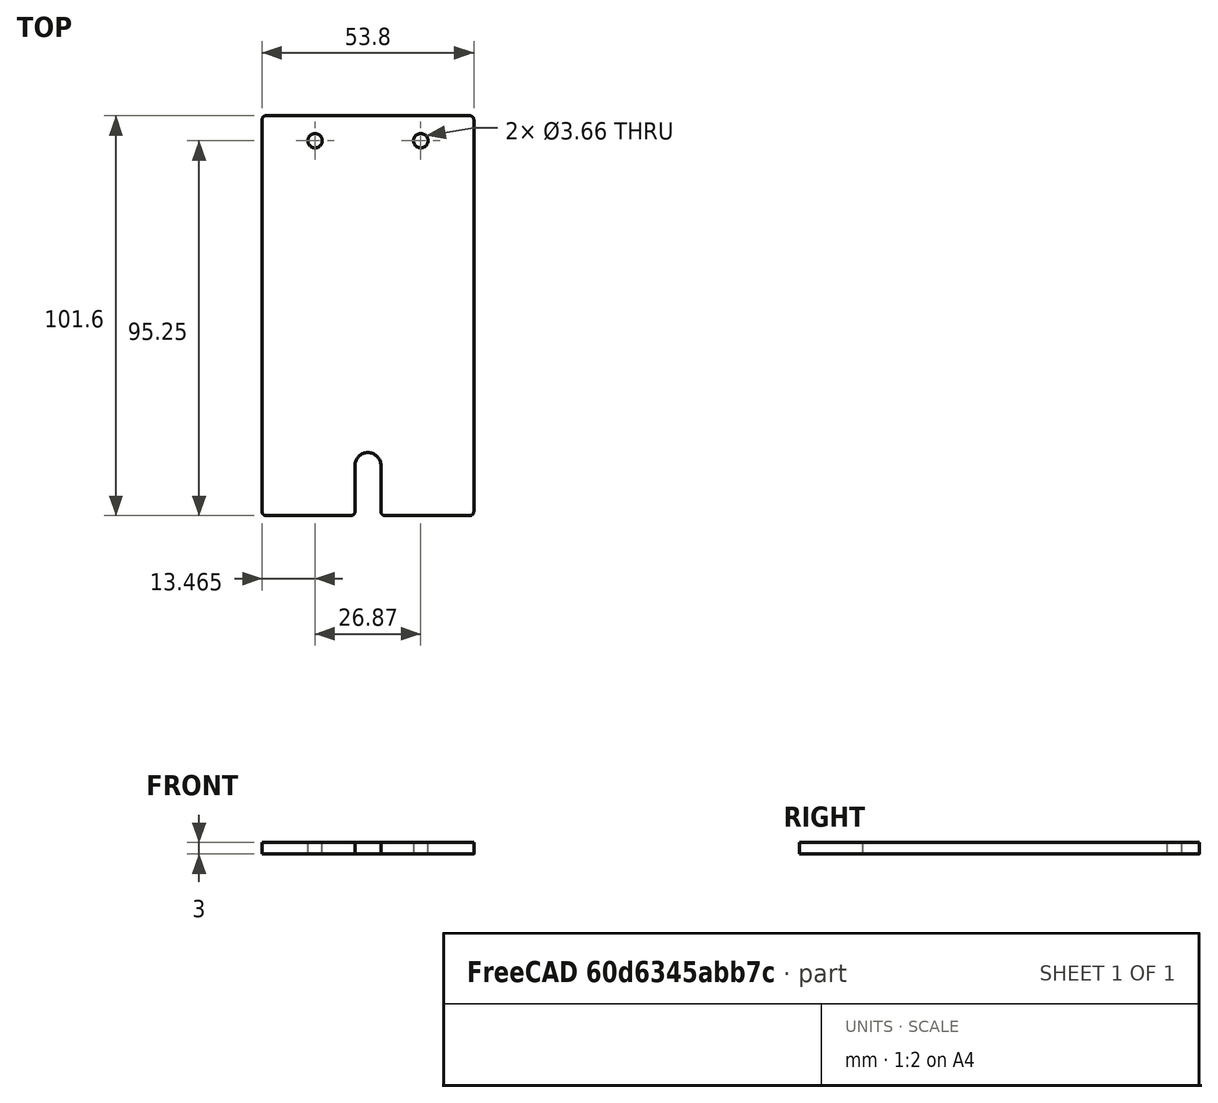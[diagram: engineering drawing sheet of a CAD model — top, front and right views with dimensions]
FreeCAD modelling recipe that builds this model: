
FCSTD DOCUMENT  (FreeCAD 0.21R33675 (Git))
Label: feeding_box_front
License: All rights reserved
LicenseURL: http://en.wikipedia.org/wiki/All_rights_reserved
objects: Sketcher::SketchObject×1, Spreadsheet::Sheet×1, PartDesign::Pad×1, PartDesign::Body×1
note: 4 computed .brp shape members not serialized (recipe doc carries the construction recipe); baked Part::Feature solids carry a one-line shape summary decoded from their .brp

FEATURE [Sketcher::SketchObject] Sketch
  FullyConstrained = true
  MapMode = 5
  Support = -> [XY_Plane]
  expr: Constraints[19] = Spreadsheet.FilletRadius
  expr: Constraints[21] = Spreadsheet.Height
  expr: Constraints[22] = Spreadsheet.Length
  expr: Constraints[26] = Spreadsheet.MountHoleDistanceFromBottom
  expr: Constraints[27] = Spreadsheet.MountHoleDiameter
  expr: Constraints[31] = Spreadsheet.BracketHoleFromSide
  expr: Constraints[32] = Spreadsheet.UpperBracketHoleFromTop
  expr: Constraints[41] = Spreadsheet.BracketHoleDiameter
  expr: Constraints[68] = Spreadsheet.BracketHoleFromSide
  expr: Constraints[72] = Spreadsheet.UpperBracketHoleFromTop
  expr: Constraints[74] = Spreadsheet.BracketHoleDiameter
  sketch-geometry (30):
    g0: ArcOfCircle CenterX=-25.9 CenterY=49.8 CenterZ=0 NormalX=0 NormalY=0 NormalZ=1 AngleXU=0 Radius=1 StartAngle=1.5708 EndAngle=3.14159
    g1: LineSegment StartX=-25.9 StartY=50.8 StartZ=0 EndX=25.9 EndY=50.8 EndZ=0
    g2: ArcOfCircle CenterX=25.9 CenterY=49.8 CenterZ=0 NormalX=0 NormalY=0 NormalZ=1 AngleXU=0 Radius=1 StartAngle=1.4e-15 EndAngle=1.5708
    g3: LineSegment StartX=26.9 StartY=49.8 StartZ=0 EndX=26.9 EndY=-49.8 EndZ=0
    g4: ArcOfCircle CenterX=25.9 CenterY=-49.8 CenterZ=0 NormalX=0 NormalY=0 NormalZ=1 AngleXU=0 Radius=1 StartAngle=4.71239 EndAngle=6.28319
    g5: LineSegment StartX=25.9 StartY=-50.8 StartZ=0 EndX=-25.9 EndY=-50.8 EndZ=0
    g6: ArcOfCircle CenterX=-25.9 CenterY=-49.8 CenterZ=0 NormalX=0 NormalY=0 NormalZ=1 AngleXU=0 Radius=1 StartAngle=3.14159 EndAngle=4.71239
    g7: LineSegment StartX=-26.9 StartY=-49.8 StartZ=0 EndX=-26.9 EndY=49.8 EndZ=0
    g8: GeomPoint X=-26.9 Y=50.8 Z=0
    g9: GeomPoint X=26.9 Y=-50.8 Z=0
    g10: Circle CenterX=0 CenterY=-38.1 CenterZ=0 NormalX=0 NormalY=0 NormalZ=1 AngleXU=0 Radius=3.302
    g11: LineSegment StartX=0 StartY=-38.1 StartZ=0 EndX=0 EndY=-50.8 EndZ=0
    g12: LineSegment StartX=-13.4352 StartY=50.8 StartZ=0 EndX=-13.4352 EndY=44.45 EndZ=0
    g13: LineSegment StartX=-13.4352 StartY=44.45 StartZ=0 EndX=-13.4352 EndY=0 EndZ=0
    g14: LineSegment StartX=-13.4352 StartY=2.6e-15 StartZ=0 EndX=-26.9 EndY=2.6e-15 EndZ=0
    g15: Circle CenterX=-13.4352 CenterY=44.45 CenterZ=0 NormalX=0 NormalY=0 NormalZ=1 AngleXU=0 Radius=1.8288
    g16: Circle CenterX=-13.4352 CenterY=2.6e-15 CenterZ=0 NormalX=0 NormalY=0 NormalZ=1 AngleXU=0 Radius=1.8288
    g17: ArcOfCircle CenterX=0 CenterY=-38.1 CenterZ=0 NormalX=0 NormalY=0 NormalZ=1 AngleXU=0 Radius=3.302 StartAngle=4e-16 EndAngle=3.14159
    g18: LineSegment StartX=-3.302 StartY=-38.1 StartZ=0 EndX=3.302 EndY=-38.1 EndZ=0
    g19: LineSegment StartX=-3.302 StartY=-38.1 StartZ=0 EndX=-3.302 EndY=-49.8 EndZ=0
    g20: LineSegment StartX=3.302 StartY=-38.1 StartZ=0 EndX=3.302 EndY=-49.8 EndZ=0
    g21: ArcOfCircle CenterX=-4.302 CenterY=-49.8 CenterZ=0 NormalX=0 NormalY=0 NormalZ=1 AngleXU=0 Radius=1 StartAngle=4.71239 EndAngle=6.28319
    g22: ArcOfCircle CenterX=4.302 CenterY=-49.8 CenterZ=0 NormalX=0 NormalY=0 NormalZ=1 AngleXU=0 Radius=1 StartAngle=3.14159 EndAngle=4.71239
    g23: LineSegment StartX=-25.9 StartY=-50.8 StartZ=0 EndX=-4.302 EndY=-50.8 EndZ=0
    g24: LineSegment StartX=4.302 StartY=-50.8 StartZ=0 EndX=25.9 EndY=-50.8 EndZ=0
    g25: LineSegment StartX=25.9 StartY=50.8 StartZ=0 EndX=26.9 EndY=50.8 EndZ=0
    g26: LineSegment StartX=26.9 StartY=49.8 StartZ=0 EndX=26.9 EndY=50.8 EndZ=0
    g27: LineSegment StartX=26.9 StartY=50.8 StartZ=0 EndX=13.4352 EndY=50.8 EndZ=0
    g28: LineSegment StartX=13.4352 StartY=50.8 StartZ=0 EndX=13.4352 EndY=44.45 EndZ=0
    g29: Circle CenterX=13.4352 CenterY=44.45 CenterZ=0 NormalX=0 NormalY=0 NormalZ=1 AngleXU=0 Radius=1.8288
  constraints (75):
    c: Tangent(g0,g1) = 1.5708
    c: Tangent(g1,g2) = 1.5708
    c: Tangent(g2,g3) = 1.5708
    c: Tangent(g3,g4) = 1.5708
    c: Tangent(g4,g5) = 1.5708
    c: Tangent(g5,g6) = 1.5708
    c: Tangent(g6,g7) = 1.5708
    c: Tangent(g7,g0) = 1.5708
    c: Horizontal(g1)
    c: Horizontal(g5)
    c: Vertical(g3)
    c: Vertical(g7)
    c: Equal(g0,g2)
    c: Equal(g2,g4)
    c: Equal(g4,g6)
    c: PointOnObject(g8,g1)
    c: PointOnObject(g8,g7)
    c: PointOnObject(g9,g3)
    c: PointOnObject(g9,g5)
    c: Radius(g2) = 1
    c: Symmetric(g8,g9,g-1)
    c: DistanceY(g4,g1) = 101.6
    c: DistanceX(g0,g2) = 53.8
    c: PointOnObject(g11,g5)
    c: PointOnObject(g11,g-2)
    c: Vertical(g11)
    c: DistanceY(g11,g11) = 12.7
    c: Diameter(g10) = 6.604
    c: Coincident(g10,g11)
    c: PointOnObject(g12,g1)
    c: Vertical(g12)
    c: DistanceX(g8,g12) = 13.4648
    c: DistanceY(g12,g12) = 6.35
    c: Coincident(g13,g12)
    c: Vertical(g13)
    c: Coincident(g14,g13)
    c: Horizontal(g14)
    c: Symmetric(g0,g6,g14)
    c: Coincident(g15,g12)
    c: Coincident(g16,g13)
    c: Equal(g15,g16)
    c: Diameter(g15) = 3.6576
    c: Coincident(g17,g10)
    c: Coincident(g18,g17)
    c: Coincident(g18,g17)
    c: Horizontal(g18)
    c: PointOnObject(g17,g18)
    c: PointOnObject(g17,g10)
    c: Coincident(g19,g17)
    c: Vertical(g19)
    c: Coincident(g20,g17)
    c: Vertical(g20)
    c: Equal(g19,g20)
    c: Tangent(g21,g19) = 1.5708
    c: Tangent(g21,g5) = 1.5708
    c: Tangent(g22,g20) = -1.5708
    c: Tangent(g22,g5) = 1.5708
    c: Equal(g22,g4)
    c: Coincident(g23,g6)
    c: Coincident(g23,g21)
    c: Coincident(g24,g22)
    c: Coincident(g24,g4)
    c: Coincident(g25,g1)
    c: Horizontal(g25)
    c: Coincident(g26,g2)
    c: Vertical(g26)
    c: Coincident(g26,g25)
    c: Coincident(g27,g25)
    c: DistanceX(g27,g27) = 13.4648
    c: Horizontal(g27)
    c: Vertical(g28)
    c: Coincident(g27,g28)
    c: DistanceY(g28,g28) = 6.35
    c: Coincident(g29,g28)
    c: Diameter(g29) = 3.6576
FEATURE [Spreadsheet::Sheet] Spreadsheet
  cells = A2='Parameters; A3='Height; B3(Height)==4 in; A4='Length; B4(Length)==53.8 mm; A5='Thickness; B5(Thickness)==3 mm; A6='FilletRadius; B6(FilletRadius)==1 mm; A7='MountHoleDiameter; B7(MountHoleDiameter)==0.26 in; A8='MountHoleDistanceFromBottom; B8(MountHoleDistanceFromBottom)==0.5 in; A10='BracketWidth; B10(BracketWidth)==0.5 in; A11='BracketHoleDiameter; B11(BracketHoleDiameter)==0.144 in; A12='BracketHoleOffset; B12(BracketHoleOffset)==0.412 in; A13='UpperBracketHoleFromTop; B13(UpperBracketHoleFromTop)==0.5 * BracketWidth; A14='BracketHoleFromSide; B14(BracketHoleFromSide)==BracketHoleOffset + Thickness
FEATURE [PartDesign::Pad] Pad
  Direction = (0,0,1)
  Length = 3
  Length2 = 10
  Profile = -> Sketch
  ReferenceAxis = -> Sketch [N_Axis]
  Type = 0
  expr: Length = Spreadsheet.Thickness
FEATURE [PartDesign::Body] Body
  Group = -> [Sketch,Pad]
  Origin = -> Origin
  Tip = -> Pad
